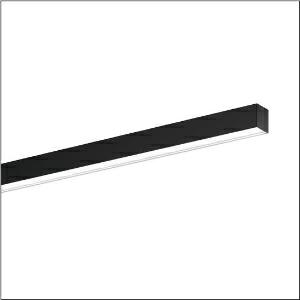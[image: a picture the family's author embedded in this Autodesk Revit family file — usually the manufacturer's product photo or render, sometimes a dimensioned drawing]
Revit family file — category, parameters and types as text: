
# Revit family: silica_r__21_51mx23tbt5b_7df7
name_source: partatom
category: Lighting Fixtures
units: mm (PartAtom-declared; Revit-internal decimal feet)

## family parameters
Cut with Voids When Loaded = No
Host = Face
Light Source = No
Part Type = Normal
Room Calculation Point = No
Round Connector Dimension = Use Diameter
Shared = No

## types (1)
- --- (1 x LED, 4030 lm, 40.5 W, 6500K)
    Apparent Load = 41 VA
    CIE Flux Codes = 78 96 99 100 100
    Color Rendering = 80
    Color Temperature = 6500K
    Default Elevation = 1800 mm
    Description = Silica® 21, office luminaire, primary optical cover: prismatic diffuser, of PMMA, CAT 2 (L<= 3000cd/m²), light emission: direct distribution, primary light characteristic: symmetric, installation type: surface-mounted, LED, rated luminous flux: 4.030lm, luminous efficacy: 95lm/W, light colour: 8tw, colour temperature: 2700..6500K, control gear: ECG DALI, with terminal, 3+2-pole, max. 2.5mm², mains connection: 220..240V, AC, 50/60Hz, rated input power: 42.6W, luminaire housing, of aluminium, jet black (RAL 9005), length: 1.504mm, width: 53mm, height: 53mm, protection rating (complete): IP20, insulation class (complete): insulation class I (protective earthing), certification: CE, permissible operating ambient temperature: 0..+35°C, standard: EN 50419, packaging unit: 1 piece
    Height = 0 mm  [stored 0 ft]
    Lamp = 1 x LED
    Lamp Light Flux = 4030 lm
    Lamp Power = 40.5 W
    Lamp count = 1
    Length = 1504 mm
    Luminous efficacy = 100 lm/W
    Manufacturer = Siteco
    ModVariant = No
    Model = 51MX23TBT5B
    Mounting Place = Ceiling
    Mounting Type = Recessed
    Number of Poles = 1
    OnlyDefault = Yes
    Power Factor = 1
    Product Name = Silica® 21
    Product group = office luminaire | ceiling recessed
    ProductGroupID = 401
    Protection Class = Protection class I
    Protection Degree = IP 20
    RLX_Detail_Level = 1
    RLX_Emergency_Light_Flux = 0 lm
    RLX_Emergency_Type = 0
    RLX_Emergency_Type_DB = No
    RlxData = <blob elided: 20473 chars, md5=35ec71d4>
    Socket = socket
    Standby Power = 0 W
    System Light Flux = 4030 lm
    System Power = 41 W
    Type Comments = individual setting
    Type Image = l_1297760.jpg
    URL = http://relux.com
    VarID = @adj_071137
    Voltage = 0 V
    Weight = 0.00 kg
    Width = 53 mm

note: [stored X ft] marks values corroborated as IEEE doubles in the binary element streams (Revit-internal decimal feet)

## geometry (parser evidence)
native form markers: Blend x4, Sweep x11
no freeform markers — native parametric forms only
